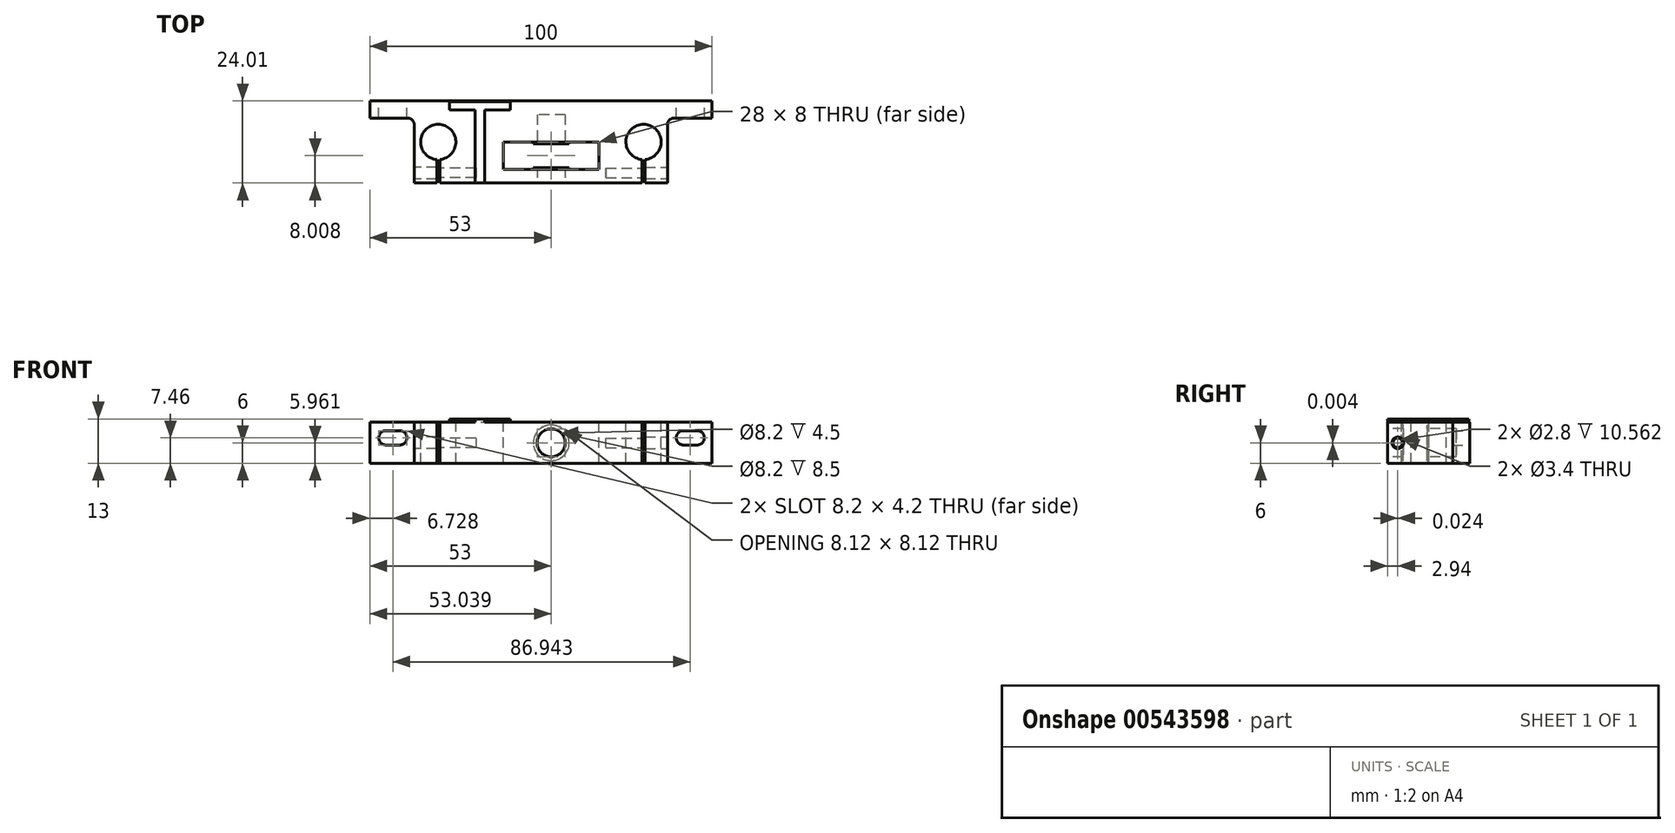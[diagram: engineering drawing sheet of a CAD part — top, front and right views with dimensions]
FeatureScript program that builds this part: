
annotation { "Feature Type Name" : "Feature", "Feature Type Description" : "" }
export const myFeature = defineFeature(function(context is Context, id is Id, definition is map)
    precondition{}
    {
        {
            var Q0;
            Q0=qCreatedBy(makeId("Top.planeOp"),FACE);
            var sketch = newSketch(context, id + "F0", { "sketchPlane" : qUnion([Q0])});
            skLineSegment(sketch, "E0", {"start": v(-46.35, 12.3) * mm, "end": v(53.65, 12.3) * mm});
            skLineSegment(sketch, "E1", {"start": v(53.65, 12.3) * mm, "end": v(53.65, 7.3) * mm});
            skLineSegment(sketch, "E2", {"start": v(53.65, 7.3) * mm, "end": v(40.65, 7.3) * mm});
            skLineSegment(sketch, "E3", {"start": v(40.65, 7.3) * mm, "end": v(40.65, -11.7) * mm});
            skLineSegment(sketch, "E4", {"start": v(40.65, -11.7) * mm, "end": v(-33.35, -11.7) * mm});
            skLineSegment(sketch, "E5", {"start": v(-33.35, -11.7) * mm, "end": v(-33.35, 7.3) * mm});
            skLineSegment(sketch, "E6", {"start": v(-33.35, 7.3) * mm, "end": v(-46.35, 7.3) * mm});
            skLineSegment(sketch, "E7", {"start": v(-46.35, 7.3) * mm, "end": v(-46.35, 12.3) * mm});
            skSolve(sketch);
        }
        {
            var Q0;
            Q0=qSketchRegion(id+"F0",true);
            extrude(context, id + "F1", {"entities" : qUnion([Q0]), "depth" : 12 * mm, "offsetDistance" : 25 * mm});
        }
        {
            var Q0;
            Q0=makeQuery(id+"F1.opExtrude","CAP_FACE",FACE,{"disambiguationData":[OSD([sQuery(id+"F0.wireOp",EDGE,"E0"),sQuery(id+"F0.wireOp",EDGE,"E1"),sQuery(id+"F0.wireOp",EDGE,"E2"),sQuery(id+"F0.wireOp",EDGE,"E3"),sQuery(id+"F0.wireOp",EDGE,"E4"),sQuery(id+"F0.wireOp",EDGE,"E5"),sQuery(id+"F0.wireOp",EDGE,"E6"),sQuery(id+"F0.wireOp",EDGE,"E7")])],"isStart":false});
            var sketch = newSketch(context, id + "F2", { "sketchPlane" : qUnion([Q0])});
            skCircle(sketch, "E8", {"center": v(-26.35, 0.3) * mm, "radius": 5.15 * mm});
            skCircle(sketch, "E9", {"center": v(33.65, 0.3) * mm, "radius": 5.15 * mm});
            skPoint(sketch, "E10", {"position": v(3.65, 12.3) * mm});
            skLineSegment(sketch, "E11.bottom", {"start": v(33.21, -3.01) * mm, "end": v(34.09, -3.01) * mm});
            skLineSegment(sketch, "E11.top", {"start": v(33.21, -12.27) * mm, "end": v(34.09, -12.27) * mm});
            skLineSegment(sketch, "E11.left", {"start": v(33.21, -3.01) * mm, "end": v(33.21, -12.27) * mm});
            skLineSegment(sketch, "E11.right", {"start": v(34.09, -3.01) * mm, "end": v(34.09, -12.27) * mm});
            skPoint(sketch, "E12", {"position": v(33.65, -3.01) * mm});
            skLineSegment(sketch, "E13", {"start": v(3.65, 12.3) * mm, "end": v(3.65, -11.7) * mm, "construction": true});
            skLineSegment(sketch, "E14.MirrorCS", {"start": v(-25.91, -12.27) * mm, "end": v(-26.79, -12.27) * mm});
            skLineSegment(sketch, "E15.MirrorCS", {"start": v(-26.79, -3.01) * mm, "end": v(-26.79, -12.27) * mm});
            skLineSegment(sketch, "E16.MirrorCS", {"start": v(-25.91, -3.01) * mm, "end": v(-26.79, -3.01) * mm});
            skLineSegment(sketch, "E17.MirrorCS", {"start": v(-25.91, -3.01) * mm, "end": v(-25.91, -12.27) * mm});
            skSolve(sketch);
        }
        {
            var Q0;
            Q0=qSketchRegion(id+"F2",true);
            var Q1;
            {var subQ3=sQuery(id+"F2.wireOp",EDGE,"E11.bottom");Q1=makeQuery(id+"F2.imprint","IMPRINT",FACE,{"disambiguationData":[TD([[makeQuery(id+"F2.imprint","IMPRINT",EDGE,{"derivedFrom":subQ3}),-1.0]])]});}
            var Q2;
            {var subQ3=sQuery(id+"F2.wireOp",EDGE,"E16.MirrorCS");Q2=makeQuery(id+"F2.imprint","IMPRINT",FACE,{"disambiguationData":[TD([[makeQuery(id+"F2.imprint","IMPRINT",EDGE,{"derivedFrom":subQ3}),1.0]])]});}
            extrude(context, id + "F3", {"entities" : qUnion([Q0, Q1, Q2]), "operationType" : NewBodyOperationType.REMOVE, "endBound" : BoundingType.THROUGH_ALL, "oppositeDirection" : true, "depth" : 25 * mm});
        }
        {
            var Q0;
            Q0=makeQuery(id+"F1.opExtrude","SWEPT_FACE",FACE,{"disambiguationData":[OSD([sQuery(id+"F0.wireOp",EDGE,"E0")])]});
            var sketch = newSketch(context, id + "F4", { "sketchPlane" : qUnion([Q0])});
            skLineSegment(sketch, "E18", {"start": v(-53.65, 7.46) * mm, "end": v(46.35, 7.46) * mm, "construction": true});
            skLineSegment(sketch, "E19.bottom", {"start": v(-49.32, 9.56) * mm, "end": v(-45.32, 9.56) * mm});
            skLineSegment(sketch, "E19.top", {"start": v(-49.32, 5.36) * mm, "end": v(-45.32, 5.36) * mm});
            skArc(sketch, "E20", {"start": v(-45.32, 5.36) * mm, "mid": v(-43.22, 7.46) * mm, "end": v(-45.32, 9.56) * mm});
            skArc(sketch, "E21", {"start": v(-49.32, 9.56) * mm, "mid": v(-51.42, 7.46) * mm, "end": v(-49.32, 5.36) * mm});
            skLineSegment(sketch, "E22.top", {"start": v(37.62, 5.36) * mm, "end": v(41.62, 5.36) * mm});
            skLineSegment(sketch, "E22.bottom", {"start": v(37.62, 9.56) * mm, "end": v(41.62, 9.56) * mm});
            skArc(sketch, "E23", {"start": v(37.62, 9.56) * mm, "mid": v(35.52, 7.46) * mm, "end": v(37.62, 5.36) * mm});
            skArc(sketch, "E24", {"start": v(41.62, 5.36) * mm, "mid": v(43.72, 7.46) * mm, "end": v(41.62, 9.56) * mm});
            skSolve(sketch);
        }
        {
            var Q0;
            Q0=qSketchRegion(id+"F4",true);
            extrude(context, id + "F5", {"entities" : qUnion([Q0]), "operationType" : NewBodyOperationType.REMOVE, "endBound" : BoundingType.THROUGH_ALL, "oppositeDirection" : true, "depth" : 25 * mm});
        }
        {
            var Q0;
            Q0=makeQuery(id+"F1.opExtrude","SWEPT_FACE",FACE,{"disambiguationData":[OSD([sQuery(id+"F0.wireOp",EDGE,"E4")])]});
            var sketch = newSketch(context, id + "F6", { "sketchPlane" : qUnion([Q0])});
            skLineSegment(sketch, "E25", {"start": v(-33.35, 6) * mm, "end": v(40.65, 6) * mm, "construction": true});
            skCircle(sketch, "E26", {"center": v(6.65, 6) * mm, "radius": 4.1 * mm});
            skSolve(sketch);
        }
        {
            var Q0;
            Q0=qSketchRegion(id+"F6",true);
            extrude(context, id + "F7", {"entities" : qUnion([Q0]), "operationType" : NewBodyOperationType.REMOVE, "oppositeDirection" : true, "depth" : 20 * mm});
        }
        {
            var Q0;
            Q0=makeQuery(id+"F1.opExtrude","CAP_FACE",FACE,{"disambiguationData":[OSD([sQuery(id+"F0.wireOp",EDGE,"E0"),sQuery(id+"F0.wireOp",EDGE,"E1"),sQuery(id+"F0.wireOp",EDGE,"E2"),sQuery(id+"F0.wireOp",EDGE,"E3"),sQuery(id+"F0.wireOp",EDGE,"E4"),sQuery(id+"F0.wireOp",EDGE,"E5"),sQuery(id+"F0.wireOp",EDGE,"E6"),sQuery(id+"F0.wireOp",EDGE,"E7")])],"isStart":false});
            var sketch = newSketch(context, id + "F8", { "sketchPlane" : qUnion([Q0])});
            skLineSegment(sketch, "E27.bottom", {"start": v(-7.35, 0.3) * mm, "end": v(20.65, 0.3) * mm});
            skLineSegment(sketch, "E27.top", {"start": v(-7.35, -7.7) * mm, "end": v(20.65, -7.7) * mm});
            skLineSegment(sketch, "E27.left", {"start": v(-7.35, 0.3) * mm, "end": v(-7.35, -7.7) * mm});
            skLineSegment(sketch, "E27.right", {"start": v(20.65, 0.3) * mm, "end": v(20.65, -7.7) * mm});
            skLineSegment(sketch, "E28", {"start": v(6.65, 12.3) * mm, "end": v(6.65, -11.7) * mm, "construction": true});
            skLineSegment(sketch, "E29", {"start": v(6.65, 0.3) * mm, "end": v(6.65, -7.7) * mm});
            skSolve(sketch);
        }
        {
            var Q0;
            Q0=qSketchRegion(id+"F8",true);
            extrude(context, id + "F9", {"entities" : qUnion([Q0]), "operationType" : NewBodyOperationType.REMOVE, "endBound" : BoundingType.THROUGH_ALL, "oppositeDirection" : true, "depth" : 25 * mm});
        }
        {
            var Q0;
            Q0=makeQuery(id+"F9.boolean.opBoolean","COPY",FACE,{"derivedFrom":makeQuery(id+"F9.opExtrude","SWEPT_FACE",FACE,{"disambiguationData":[OSD([sQuery(id+"F8.wireOp",EDGE,"E27.bottom")])]})});
            var sketch = newSketch(context, id + "F10", { "sketchPlane" : qUnion([Q0])});
            skCircle(sketch, "E30", {"center": v(6.65, 6) * mm, "radius": 5.2 * mm});
            skSolve(sketch);
        }
        {
            var Q0;
            Q0=makeQuery(id+"F10.imprint","IMPRINT",FACE,{"disambiguationData":[TD([[makeQuery(id+"F10.imprint","IMPRINT",EDGE,{"derivedFrom":sQuery(id+"F10.wireOp",EDGE,"E30")}),1.0]])]});
            extrude(context, id + "F11", {"entities" : qUnion([Q0]), "operationType" : NewBodyOperationType.ADD, "depth" : 0.5 * mm});
        }
        {
            var Q0;
            Q0=makeQuery(id+"F9.boolean.opBoolean","COPY",FACE,{"derivedFrom":makeQuery(id+"F9.opExtrude","SWEPT_FACE",FACE,{"disambiguationData":[OSD([sQuery(id+"F8.wireOp",EDGE,"E27.top")])]})});
            var sketch = newSketch(context, id + "F12", { "sketchPlane" : qUnion([Q0])});
            skCircle(sketch, "E31", {"center": v(-6.65, 6) * mm, "radius": 5.25 * mm});
            skSolve(sketch);
        }
        {
            var Q0;
            Q0=makeQuery(id+"F12.imprint","IMPRINT",FACE,{"disambiguationData":[TD([[makeQuery(id+"F12.imprint","IMPRINT",EDGE,{"derivedFrom":sQuery(id+"F12.wireOp",EDGE,"E31")}),1.0]])]});
            extrude(context, id + "F13", {"entities" : qUnion([Q0]), "operationType" : NewBodyOperationType.ADD, "depth" : 0.5 * mm});
        }
        {
            var Q0;
            Q0=makeQuery(id+"F1.opExtrude","CAP_FACE",FACE,{"disambiguationData":[OSD([sQuery(id+"F0.wireOp",EDGE,"E0"),sQuery(id+"F0.wireOp",EDGE,"E1"),sQuery(id+"F0.wireOp",EDGE,"E2"),sQuery(id+"F0.wireOp",EDGE,"E3"),sQuery(id+"F0.wireOp",EDGE,"E4"),sQuery(id+"F0.wireOp",EDGE,"E5"),sQuery(id+"F0.wireOp",EDGE,"E6"),sQuery(id+"F0.wireOp",EDGE,"E7")])],"isStart":false});
            var sketch = newSketch(context, id + "F14", { "sketchPlane" : qUnion([Q0])});
            skText(sketch, "E32", { "text": "T", "fontName": "OpenSans-Regular.ttf"});
            const initialGuessF14  = {"E32": [-0.02337, -0.0117, 1, 0, 0.024]};
            skSetInitialGuess(sketch, initialGuessF14);
            skSolve(sketch);
        }
        {
            var Q0;
            Q0=qSketchRegion(id+"F14",true);
            extrude(context, id + "F15", {"entities" : qUnion([Q0]), "operationType" : NewBodyOperationType.ADD, "depth" : 1 * mm});
        }
        {
            var Q0;
            Q0=makeQuery(id+"F1.opExtrude","SWEPT_FACE",FACE,{"disambiguationData":[OSD([sQuery(id+"F0.wireOp",EDGE,"E3")])]});
            var sketch = newSketch(context, id + "F16", { "sketchPlane" : qUnion([Q0])});
            skCircle(sketch, "E33", {"center": v(-8.74, 6) * mm, "radius": 1.7 * mm});
            skCircle(sketch, "E34", {"center": v(-8.74, 6) * mm, "radius": 1.4 * mm});
            skLineSegment(sketch, "E35", {"start": v(-11.7, 6) * mm, "end": v(-3.84, 6) * mm, "construction": true});
            skSolve(sketch);
        }
        {
            var Q0;
            Q0=makeQuery(id+"F16.imprint","IMPRINT",FACE,{"disambiguationData":[TD([[makeQuery(id+"F16.imprint","IMPRINT",EDGE,{"derivedFrom":sQuery(id+"F16.wireOp",EDGE,"E34")}),1.0]])]});
            extrude(context, id + "F17", {"entities" : qUnion([Q0]), "operationType" : NewBodyOperationType.REMOVE, "oppositeDirection" : true, "depth" : 18 * mm});
        }
        {
            var Q0;
            Q0=makeQuery(id+"F16.imprint","IMPRINT",FACE,{"disambiguationData":[TD([[makeQuery(id+"F16.imprint","IMPRINT",EDGE,{"derivedFrom":sQuery(id+"F16.wireOp",EDGE,"E34")}),1.0]])]});
            var Q1;
            Q1=makeQuery(id+"F16.imprint","IMPRINT",FACE,{"disambiguationData":[TD([[makeQuery(id+"F16.imprint","IMPRINT",EDGE,{"derivedFrom":sQuery(id+"F16.wireOp",EDGE,"E33")}),1.0]])]});
            extrude(context, id + "F18", {"entities" : qUnion([Q0, Q1]), "operationType" : NewBodyOperationType.REMOVE, "endBound" : BoundingType.UP_TO_NEXT, "oppositeDirection" : true, "depth" : 7 * mm});
        }
        {
            var Q0;
            Q0=makeQuery(id+"F1.opExtrude","SWEPT_EDGE",EDGE,{"disambiguationData":[OSD([sQuery(id+"F0.wireOp",EDGE,"E2"),sQuery(id+"F0.wireOp",EDGE,"E3")])]});
            fillet(context, id + "F19", {"entities" : qUnion([Q0]), "radius" : 2 * mm, "tangentPropagation" : true, "allowEdgeOverflow" : false});
        }
        {
            var Q0;
            Q0=makeQuery(id+"F1.opExtrude","SWEPT_FACE",FACE,{"disambiguationData":[OSD([sQuery(id+"F0.wireOp",EDGE,"E5")])]});
            var sketch = newSketch(context, id + "F20", { "sketchPlane" : qUnion([Q0])});
            skCircle(sketch, "E36", {"center": v(8.76, 6) * mm, "radius": 1.7 * mm});
            skCircle(sketch, "E37", {"center": v(8.76, 6) * mm, "radius": 1.4 * mm});
            skLineSegment(sketch, "E38", {"start": v(8.76, 0) * mm, "end": v(8.76, 12) * mm, "construction": true});
            skSolve(sketch);
        }
        {
            var Q0;
            Q0=makeQuery(id+"F20.imprint","IMPRINT",FACE,{"disambiguationData":[TD([[makeQuery(id+"F20.imprint","IMPRINT",EDGE,{"derivedFrom":sQuery(id+"F20.wireOp",EDGE,"E37")}),1.0]])]});
            extrude(context, id + "F21", {"entities" : qUnion([Q0]), "operationType" : NewBodyOperationType.REMOVE, "oppositeDirection" : true, "depth" : 18 * mm});
        }
        {
            var Q0;
            Q0=makeQuery(id+"F20.imprint","IMPRINT",FACE,{"disambiguationData":[TD([[makeQuery(id+"F20.imprint","IMPRINT",EDGE,{"derivedFrom":sQuery(id+"F20.wireOp",EDGE,"E37")}),1.0]])]});
            var Q1;
            Q1=makeQuery(id+"F20.imprint","IMPRINT",FACE,{"disambiguationData":[TD([[makeQuery(id+"F20.imprint","IMPRINT",EDGE,{"derivedFrom":sQuery(id+"F20.wireOp",EDGE,"E36")}),1.0]])]});
            extrude(context, id + "F22", {"entities" : qUnion([Q0, Q1]), "operationType" : NewBodyOperationType.REMOVE, "endBound" : BoundingType.UP_TO_NEXT, "oppositeDirection" : true, "depth" : 25 * mm});
        }
        {
            var Q0;
            Q0=makeQuery(id+"F1.opExtrude","SWEPT_EDGE",EDGE,{"disambiguationData":[OSD([sQuery(id+"F0.wireOp",EDGE,"E5"),sQuery(id+"F0.wireOp",EDGE,"E6")])]});
            fillet(context, id + "F23", {"entities" : qUnion([Q0]), "radius" : 2 * mm, "tangentPropagation" : true, "allowEdgeOverflow" : false});
        }
    });
